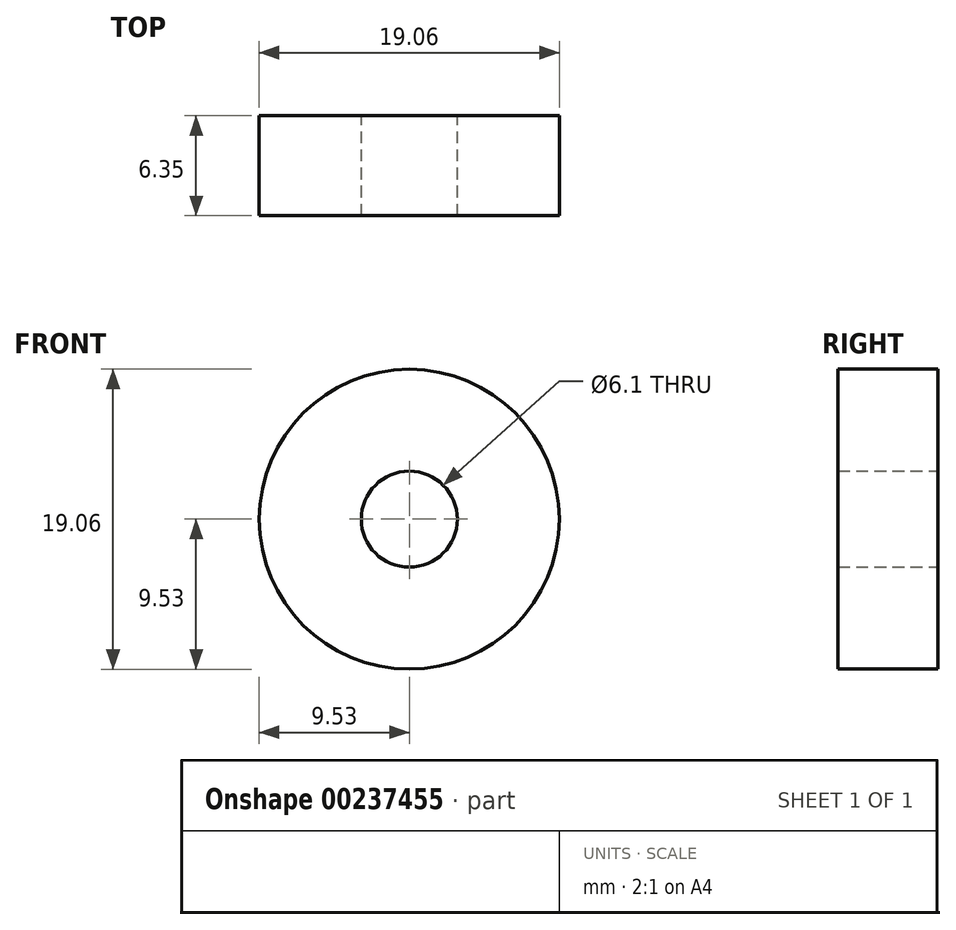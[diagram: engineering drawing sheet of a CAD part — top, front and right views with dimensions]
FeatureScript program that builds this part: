
annotation { "Feature Type Name" : "Feature", "Feature Type Description" : "" }
export const myFeature = defineFeature(function(context is Context, id is Id, definition is map)
    precondition{}
    {
        {
            var Q0;
            Q0=qCreatedBy(makeId("Front.planeOp"),FACE);
            var sketch = newSketch(context, id + "F0", { "sketchPlane" : qUnion([Q0])});
            skCircle(sketch, "E0", {"center": v(0, 0) * mm, "radius": 9.53 * mm});
            skCircle(sketch, "E1", {"center": v(0, 0) * mm, "radius": 3.05 * mm});
            skSolve(sketch);
        }
        {
            var Q0;
            Q0 = qSketchRegion(id + "F0", true);
            extrude(context, id + "F1", {"entities" : qUnion([Q0]), "depth" : 6.35 * mm});
        }
    });
